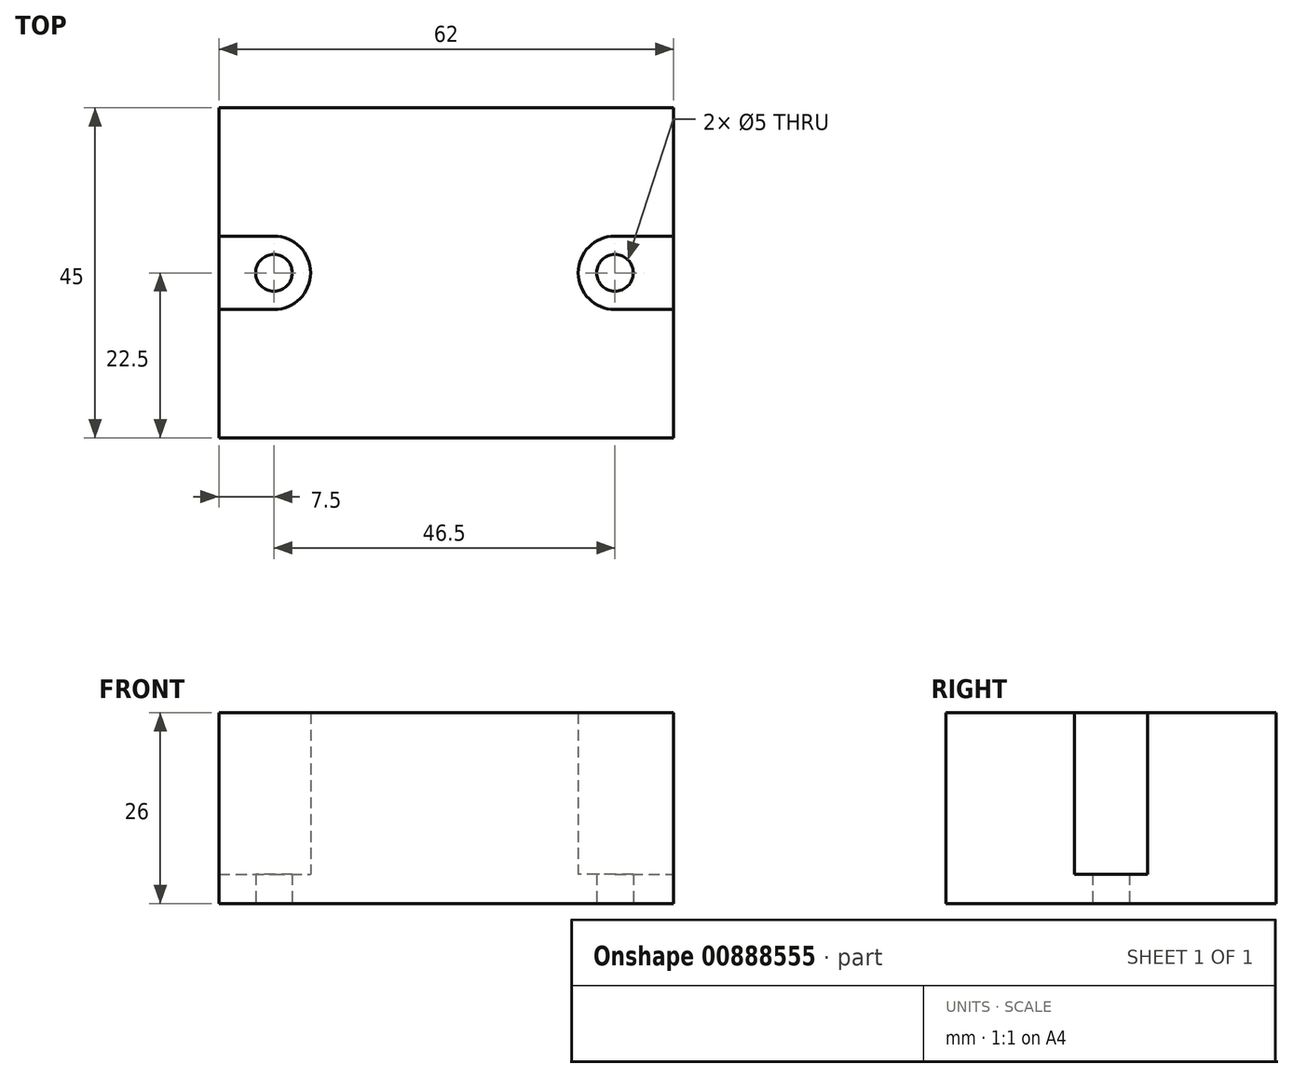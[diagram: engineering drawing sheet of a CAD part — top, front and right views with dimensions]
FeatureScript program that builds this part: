
annotation { "Feature Type Name" : "Feature", "Feature Type Description" : "" }
export const myFeature = defineFeature(function(context is Context, id is Id, definition is map)
    precondition{}
    {
        {
            var Q0;
            Q0=qCreatedBy(makeId("Top.planeOp"),FACE);
            var sketch = newSketch(context, id + "F0", { "sketchPlane" : qUnion([Q0])});
            skLineSegment(sketch, "E0.bottom", {"start": v(0, 0) * mm, "end": v(62, 0) * mm});
            skLineSegment(sketch, "E0.top", {"start": v(0, 45) * mm, "end": v(62, 45) * mm});
            skLineSegment(sketch, "E0.left", {"start": v(0, 0) * mm, "end": v(0, 45) * mm});
            skLineSegment(sketch, "E0.right", {"start": v(62, 0) * mm, "end": v(62, 45) * mm});
            skCircle(sketch, "E1", {"center": v(54, 22.5) * mm, "radius": 2.5 * mm});
            skPoint(sketch, "E1.centerSnap0", {"position": v(62, 22.5) * mm});
            skCircle(sketch, "E2", {"center": v(7.5, 22.5) * mm, "radius": 2.5 * mm});
            skPoint(sketch, "E2.centerSnap0", {"position": v(0, 22.5) * mm});
            skSolve(sketch);
        }
        {
            var Q0;
            Q0 = qSketchRegion(id + "F0", true);
            extrude(context, id + "F1", {"entities" : qUnion([Q0]), "depth" : 4 * mm, "offsetDistance" : 25 * mm});
        }
        {
            var Q0;
            Q0=makeQuery(id+"F1.opExtrude","CAP_FACE",FACE,{"disambiguationData":[OSD([sQuery(id+"F0.wireOp",EDGE,"E0.bottom"),sQuery(id+"F0.wireOp",EDGE,"E0.top"),sQuery(id+"F0.wireOp",EDGE,"E0.left"),sQuery(id+"F0.wireOp",EDGE,"E0.right"),sQuery(id+"F0.wireOp",EDGE,"E1"),sQuery(id+"F0.wireOp",EDGE,"E2")])],"isStart":false});
            var sketch = newSketch(context, id + "F2", { "sketchPlane" : qUnion([Q0])});
            skLineSegment(sketch, "E3", {"start": v(0, 45) * mm, "end": v(0, 27.5) * mm});
            skLineSegment(sketch, "E4", {"start": v(0, 27.5) * mm, "end": v(7.5, 27.5) * mm});
            skArc(sketch, "E5", {"start": v(12.5, 22.5) * mm, "mid": v(11.04, 26.04) * mm, "end": v(7.5, 27.5) * mm});
            skArc(sketch, "E6", {"start": v(54, 27.5) * mm, "mid": v(50.46, 26.04) * mm, "end": v(49, 22.5) * mm});
            skLineSegment(sketch, "E7", {"start": v(54, 27.5) * mm, "end": v(62, 27.5) * mm});
            skLineSegment(sketch, "E8", {"start": v(62, 27.5) * mm, "end": v(62, 45) * mm});
            skLineSegment(sketch, "E9", {"start": v(62, 45) * mm, "end": v(0, 45) * mm});
            skLineSegment(sketch, "E10", {"start": v(12.5, 22.5) * mm, "end": v(49, 22.5) * mm, "construction": true});
            skArc(sketch, "E11.MirrorCS", {"start": v(12.5, 22.5) * mm, "mid": v(11.04, 18.96) * mm, "end": v(7.5, 17.5) * mm});
            skLineSegment(sketch, "E12.MirrorCS", {"start": v(0, 17.5) * mm, "end": v(7.5, 17.5) * mm});
            skLineSegment(sketch, "E13.MirrorCS", {"start": v(0, 0) * mm, "end": v(0, 17.5) * mm});
            skLineSegment(sketch, "E14.MirrorCS", {"start": v(62, 0) * mm, "end": v(0, 0) * mm});
            skLineSegment(sketch, "E15.MirrorCS", {"start": v(62, 17.5) * mm, "end": v(62, 0) * mm});
            skLineSegment(sketch, "E16.MirrorCS", {"start": v(54, 17.5) * mm, "end": v(62, 17.5) * mm});
            skArc(sketch, "E17.MirrorCS", {"start": v(54, 17.5) * mm, "mid": v(50.46, 18.96) * mm, "end": v(49, 22.5) * mm});
            skSolve(sketch);
        }
        {
            var Q0;
            Q0 = qSketchRegion(id + "F2", true);
            extrude(context, id + "F3", {"entities" : qUnion([Q0]), "operationType" : NewBodyOperationType.ADD, "depth" : 22 * mm, "offsetDistance" : 25 * mm});
        }
    });
